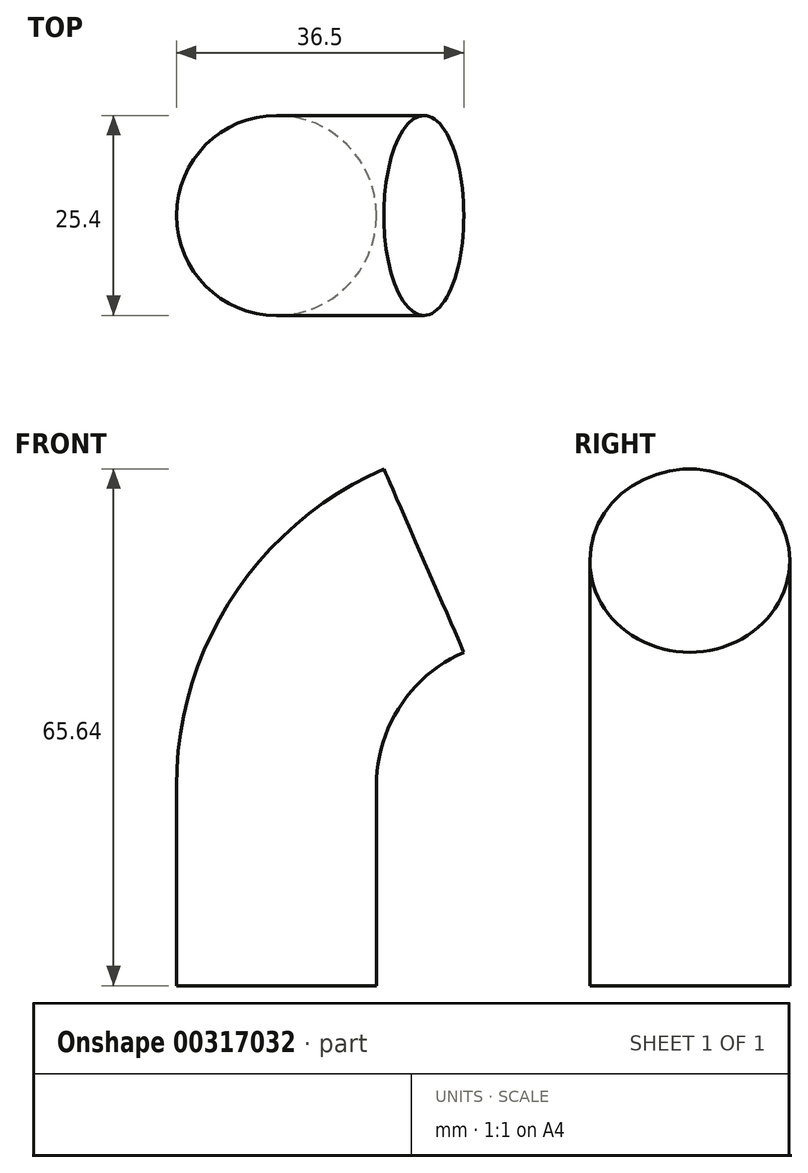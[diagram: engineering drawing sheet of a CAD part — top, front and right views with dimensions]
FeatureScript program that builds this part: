
annotation { "Feature Type Name" : "Feature", "Feature Type Description" : "" }
export const myFeature = defineFeature(function(context is Context, id is Id, definition is map)
    precondition{}
    {
        {
            var Q0;
            Q0=qCreatedBy(makeId("Front.planeOp"),FACE);
            var sketch = newSketch(context, id + "F0", { "sketchPlane" : qUnion([Q0])});
            skLineSegment(sketch, "E0", {"start": v(0, 0) * mm, "end": v(0, 25.4) * mm});
            skArc(sketch, "E1", {"start": v(18.72, 54) * mm, "mid": v(5.1, 42.5) * mm, "end": v(0, 25.4) * mm});
            skSolve(sketch);
        }
        {
            var Q0;
            Q0=qCreatedBy(makeId("Top.planeOp"),FACE);
            var sketch = newSketch(context, id + "F1", { "sketchPlane" : qUnion([Q0])});
            skCircle(sketch, "E2", {"center": v(0, 0) * mm, "radius": 12.7 * mm});
            skSolve(sketch);
        }
        {
            var Q0;
            Q0 = qSketchRegion(id + "F1", true);
            var Q1;
            Q1 = qConstructionFilter(qBodyType(qCreatedBy(id + "F0" ,EDGE), BodyType.WIRE), ConstructionObject.NO);
            sweep(context, id + "F2", {"profiles" : qUnion([Q0]), "path" : qUnion([Q1])});
        }
    });
